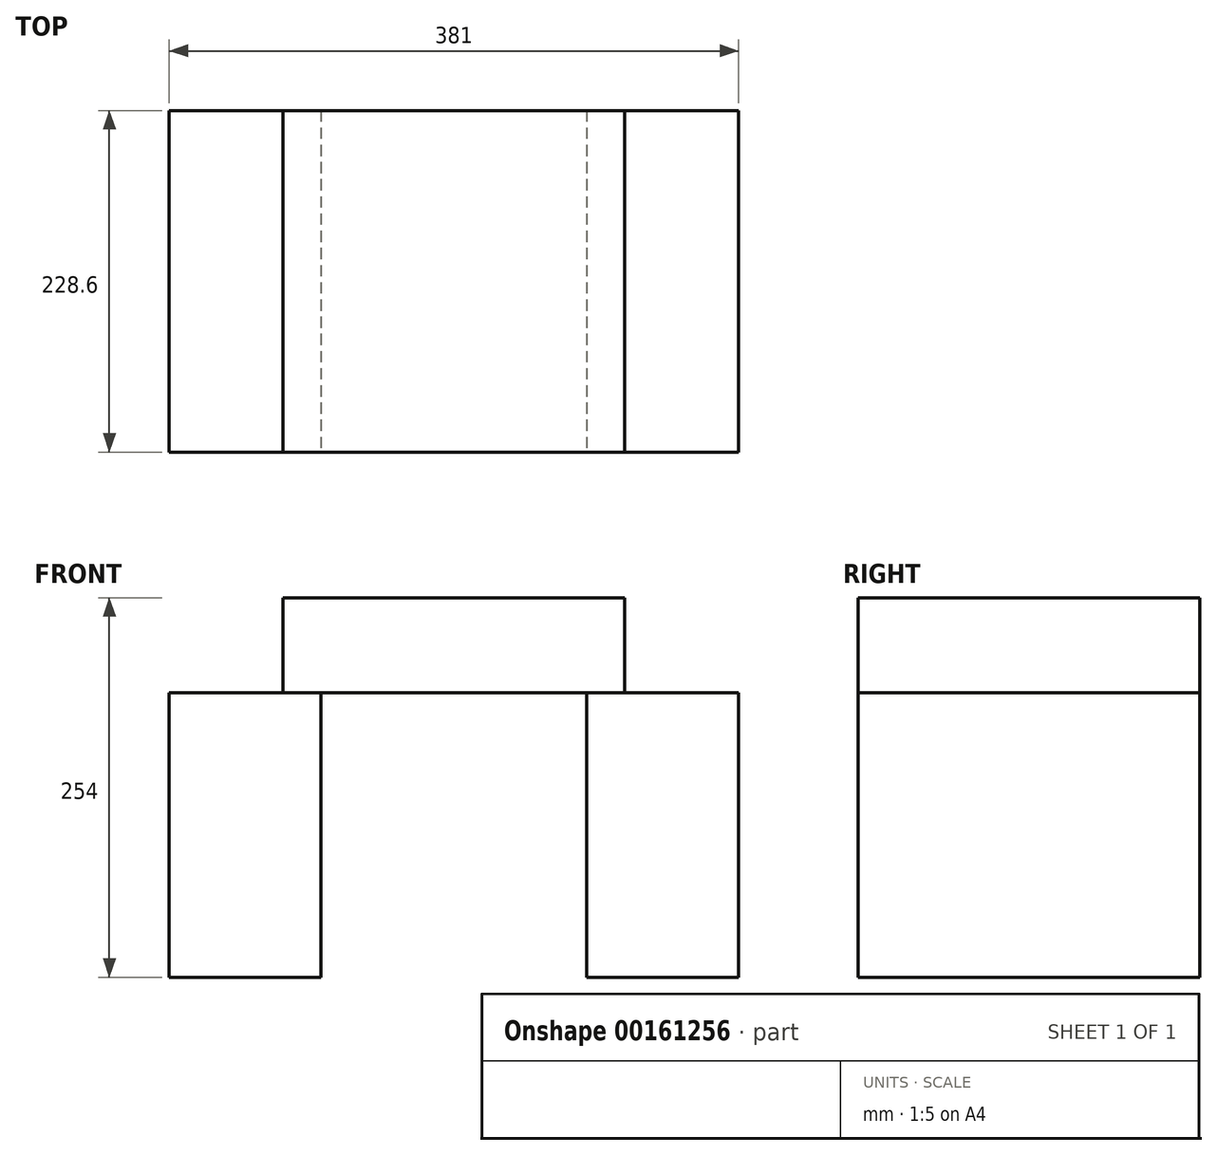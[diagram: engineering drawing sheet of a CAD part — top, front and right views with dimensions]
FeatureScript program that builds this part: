
annotation { "Feature Type Name" : "Feature", "Feature Type Description" : "" }
export const myFeature = defineFeature(function(context is Context, id is Id, definition is map)
    precondition{}
    {
        {
            var Q0;
            Q0=qCreatedBy(makeId("Front.planeOp"),FACE);
            var sketch = newSketch(context, id + "F0", { "sketchPlane" : qUnion([Q0])});
            skLineSegment(sketch, "E0.bottom", {"start": v(-190.5, 0) * mm, "end": v(-88.9, 0) * mm});
            skLineSegment(sketch, "E0.top", {"start": v(-190.5, 190.5) * mm, "end": v(-88.9, 190.5) * mm});
            skLineSegment(sketch, "E0.left", {"start": v(-190.5, 0) * mm, "end": v(-190.5, 190.5) * mm});
            skLineSegment(sketch, "E0.right", {"start": v(-88.9, 0) * mm, "end": v(-88.9, 190.5) * mm});
            skLineSegment(sketch, "E1", {"start": v(-190.5, 63.5) * mm, "end": v(-88.9, 63.5) * mm});
            skLineSegment(sketch, "E2", {"start": v(-190.5, 127) * mm, "end": v(-88.9, 127) * mm});
            skLineSegment(sketch, "E3", {"start": v(0, 0) * mm, "end": v(0, 179.25) * mm, "construction": true});
            skLineSegment(sketch, "E4.MirrorCS", {"start": v(190.5, 127) * mm, "end": v(88.9, 127) * mm});
            skLineSegment(sketch, "E5.MirrorCS", {"start": v(88.9, 0) * mm, "end": v(88.9, 190.5) * mm});
            skLineSegment(sketch, "E6.MirrorCS", {"start": v(190.5, 190.5) * mm, "end": v(88.9, 190.5) * mm});
            skLineSegment(sketch, "E7.MirrorCS", {"start": v(190.5, 0) * mm, "end": v(88.9, 0) * mm});
            skLineSegment(sketch, "E8.MirrorCS", {"start": v(190.5, 0) * mm, "end": v(190.5, 190.5) * mm});
            skLineSegment(sketch, "E9.MirrorCS", {"start": v(190.5, 63.5) * mm, "end": v(88.9, 63.5) * mm});
            skSolve(sketch);
        }
        {
            var Q0;
            Q0 = qSketchRegion(id + "F0", true);
            extrude(context, id + "F1", {"entities" : qUnion([Q0]), "oppositeDirection" : true, "depth" : 228.6 * mm});
        }
        {
            var Q0;
            Q0=makeQuery(id+"F1.opExtrude","SWEPT_FACE",FACE,{"disambiguationData":[OSD([sQuery(id+"F0.wireOp",EDGE,"E0.top")])]});
            var sketch = newSketch(context, id + "F2", { "sketchPlane" : qUnion([Q0])});
            skLineSegment(sketch, "E10.bottom", {"start": v(-114.3, 114.3) * mm, "end": v(114.3, 114.3) * mm});
            skLineSegment(sketch, "E10.top", {"start": v(-114.3, 0) * mm, "end": v(114.3, 0) * mm});
            skLineSegment(sketch, "E10.left", {"start": v(-114.3, 114.3) * mm, "end": v(-114.3, 0) * mm});
            skLineSegment(sketch, "E10.right", {"start": v(114.3, 114.3) * mm, "end": v(114.3, 0) * mm});
            skLineSegment(sketch, "E11", {"start": v(0, 0) * mm, "end": v(0, 255.78) * mm, "construction": true});
            skLineSegment(sketch, "E12.top", {"start": v(-114.3, 228.6) * mm, "end": v(114.3, 228.6) * mm});
            skLineSegment(sketch, "E12.left", {"start": v(-114.3, 114.3) * mm, "end": v(-114.3, 228.6) * mm});
            skLineSegment(sketch, "E12.right", {"start": v(114.3, 114.3) * mm, "end": v(114.3, 228.6) * mm});
            skSolve(sketch);
        }
        {
            var Q0;
            Q0 = qSketchRegion(id + "F2", true);
            extrude(context, id + "F3", {"entities" : qUnion([Q0]), "depth" : 63.5 * mm});
        }
    });
